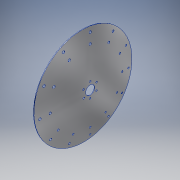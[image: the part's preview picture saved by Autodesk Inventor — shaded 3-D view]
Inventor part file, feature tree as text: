
AUTODESK INVENTOR PART (.ipt)
format: ipt  version: 2019 (Build 230136000, 136)  size: 158,208 bytes
history: native  units: in
note: dims shown in document units (in); Inventor stores cm internally (conversion verified against a paired STEP export)
features: extrude x2, sketch x2
ambient origin geometry x8: Origin, YZ Plane, XZ Plane, XY Plane, X Axis, Y Axis, Z Axis, Center Point
bodies: Solid1 (feature_tree)
feature tree (4):
  extrude  "Extrusion1"  Depth=0.5in
  extrude  "Extrusion2"  Depth=0.0625in
  sketch  "Sketch1"  dims[d0=12.0in d1=0.5in]
  sketch  "Sketch2"  dims[d2=1.0in d3=0.25in d4=4.7244in d6=360.0deg d8=0.0625in d9=0.0in d10=1.14in d11=0.204in d12=1.875in d13=2.3622in d15=360.0deg d17=1.0in d18=0.0in]
